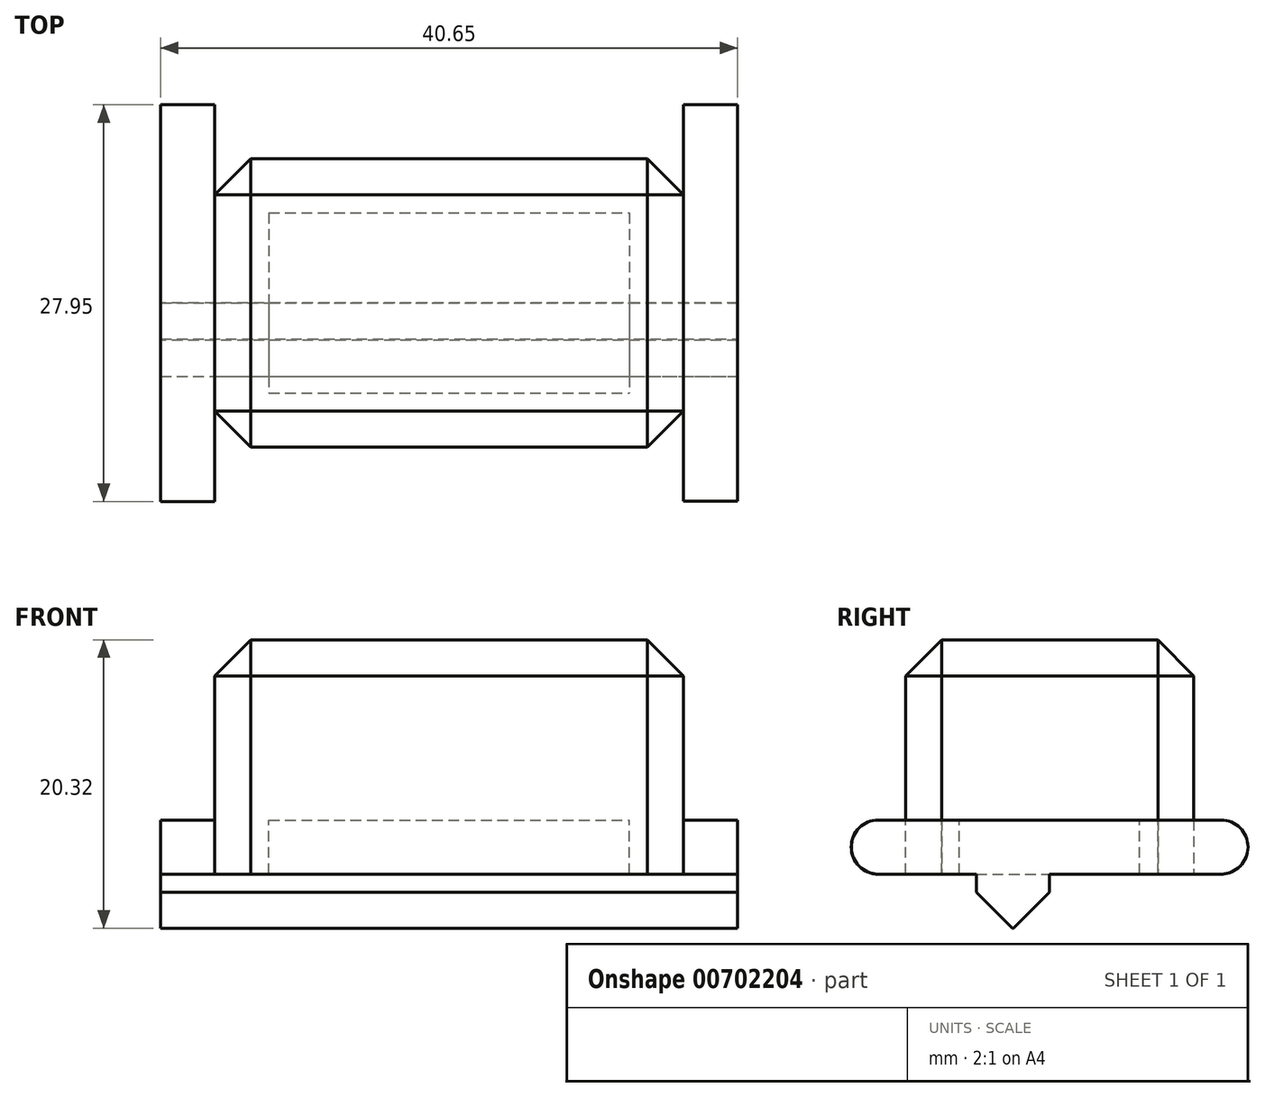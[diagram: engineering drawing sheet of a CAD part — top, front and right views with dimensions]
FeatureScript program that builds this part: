
annotation { "Feature Type Name" : "Feature", "Feature Type Description" : "" }
export const myFeature = defineFeature(function(context is Context, id is Id, definition is map)
    precondition{}
    {
        {
            var Q0;
            Q0=qCreatedBy(makeId("Top.planeOp"),FACE);
            var sketch = newSketch(context, id + "F0", { "sketchPlane" : qUnion([Q0])});
            skLineSegment(sketch, "E0.bottom", {"start": v(0, 0) * mm, "end": v(33.02, 0) * mm});
            skLineSegment(sketch, "E0.top", {"start": v(0, -20.32) * mm, "end": v(33.02, -20.32) * mm});
            skLineSegment(sketch, "E0.left", {"start": v(0, 0) * mm, "end": v(0, -20.32) * mm});
            skLineSegment(sketch, "E0.right", {"start": v(33.02, 0) * mm, "end": v(33.02, -20.32) * mm});
            skLineSegment(sketch, "E1", {"start": v(0, 0) * mm, "end": v(3.81, 0) * mm});
            skLineSegment(sketch, "E2.bottom", {"start": v(3.81, -3.81) * mm, "end": v(29.21, -3.81) * mm});
            skLineSegment(sketch, "E2.top", {"start": v(3.81, -16.51) * mm, "end": v(29.21, -16.51) * mm});
            skLineSegment(sketch, "E2.left", {"start": v(3.81, -3.81) * mm, "end": v(3.81, -16.51) * mm});
            skLineSegment(sketch, "E2.right", {"start": v(29.21, -3.8) * mm, "end": v(29.21, -16.51) * mm});
            skSolve(sketch);
        }
        {
            var Q0;
            Q0 = qSketchRegion(id + "F0", true);
            extrude(context, id + "F1", {"entities" : qUnion([Q0]), "oppositeDirection" : true, "depth" : 3.8 * mm, "offsetDistance" : 25.4 * mm});
        }
        {
            var Q0;
            Q0=qCreatedBy(makeId("Top.planeOp"),FACE);
            var sketch = newSketch(context, id + "F2", { "sketchPlane" : qUnion([Q0])});
            skLineSegment(sketch, "E3.bottom", {"start": v(0, 0) * mm, "end": v(33.02, 0) * mm});
            skLineSegment(sketch, "E3.top", {"start": v(0, -20.32) * mm, "end": v(33.02, -20.32) * mm});
            skLineSegment(sketch, "E3.left", {"start": v(0, 0) * mm, "end": v(0, -20.32) * mm});
            skLineSegment(sketch, "E3.right", {"start": v(33.02, 0) * mm, "end": v(33.02, -20.32) * mm});
            skSolve(sketch);
        }
        {
            var Q0;
            Q0 = qSketchRegion(id + "F2", true);
            extrude(context, id + "F3", {"entities" : qUnion([Q0]), "operationType" : NewBodyOperationType.ADD, "depth" : 12.7 * mm, "offsetDistance" : 25.4 * mm});
        }
        {
            var Q0;
            Q0=makeQuery(id+"F3.opExtrude","CAP_EDGE",EDGE,{"disambiguationData":[OSD([sQuery(id+"F2.wireOp",EDGE,"E3.bottom")])],"isStart":false});
            var Q1;
            Q1=makeQuery(id+"F3.opExtrude","CAP_EDGE",EDGE,{"disambiguationData":[OSD([sQuery(id+"F2.wireOp",EDGE,"E3.right")])],"isStart":false});
            var Q2;
            Q2=makeQuery(id+"F3.opExtrude","CAP_EDGE",EDGE,{"disambiguationData":[OSD([sQuery(id+"F2.wireOp",EDGE,"E3.top")])],"isStart":false});
            var Q3;
            Q3=makeQuery(id+"F3.opExtrude","CAP_EDGE",EDGE,{"disambiguationData":[OSD([sQuery(id+"F2.wireOp",EDGE,"E3.left")])],"isStart":false});
            var Q4;
            Q4=makeQuery(id+"F3.boolean.opBoolean","MERGE",EDGE,{"derivedFrom":[makeQuery(id+"F1.opExtrude","SWEPT_EDGE",EDGE,{"disambiguationData":[OSD([sQuery(id+"F0.wireOp",EDGE,"E0.bottom"),sQuery(id+"F0.wireOp",EDGE,"E0.right")])]}),makeQuery(id+"F3.opExtrude","SWEPT_EDGE",EDGE,{"disambiguationData":[OSD([sQuery(id+"F2.wireOp",EDGE,"E3.bottom"),sQuery(id+"F2.wireOp",EDGE,"E3.right")])]})]});
            var Q5;
            Q5=makeQuery(id+"F3.boolean.opBoolean","MERGE",EDGE,{"derivedFrom":[makeQuery(id+"F1.opExtrude","SWEPT_EDGE",EDGE,{"disambiguationData":[OSD([sQuery(id+"F0.wireOp",EDGE,"E0.left"),sQuery(id+"F0.wireOp",EDGE,"E1")])]}),makeQuery(id+"F3.opExtrude","SWEPT_EDGE",EDGE,{"disambiguationData":[OSD([sQuery(id+"F2.wireOp",EDGE,"E3.bottom"),sQuery(id+"F2.wireOp",EDGE,"E3.left")])]})]});
            var Q6;
            Q6=makeQuery(id+"F3.boolean.opBoolean","MERGE",EDGE,{"derivedFrom":[makeQuery(id+"F1.opExtrude","SWEPT_EDGE",EDGE,{"disambiguationData":[OSD([sQuery(id+"F0.wireOp",EDGE,"E0.top"),sQuery(id+"F0.wireOp",EDGE,"E0.right")])]}),makeQuery(id+"F3.opExtrude","SWEPT_EDGE",EDGE,{"disambiguationData":[OSD([sQuery(id+"F2.wireOp",EDGE,"E3.top"),sQuery(id+"F2.wireOp",EDGE,"E3.right")])]})]});
            var Q7;
            Q7=makeQuery(id+"F3.boolean.opBoolean","MERGE",EDGE,{"derivedFrom":[makeQuery(id+"F1.opExtrude","SWEPT_EDGE",EDGE,{"disambiguationData":[OSD([sQuery(id+"F0.wireOp",EDGE,"E0.top"),sQuery(id+"F0.wireOp",EDGE,"E0.left")])]}),makeQuery(id+"F3.opExtrude","SWEPT_EDGE",EDGE,{"disambiguationData":[OSD([sQuery(id+"F2.wireOp",EDGE,"E3.top"),sQuery(id+"F2.wireOp",EDGE,"E3.left")])]})]});
            chamfer(context, id + "F4", {"entities" : qUnion([Q0, Q1, Q2, Q3, Q4, Q5, Q6, Q7]), "width" : 2.54 * mm, "tangentPropagation" : true});
        }
        {
            var Q0;
            Q0=makeQuery(id+"F3.boolean.opBoolean","MERGE",FACE,{"derivedFrom":[makeQuery(id+"F1.opExtrude","SWEPT_FACE",FACE,{"disambiguationData":[OSD([sQuery(id+"F0.wireOp",EDGE,"E0.left")])]}),makeQuery(id+"F3.opExtrude","SWEPT_FACE",FACE,{"disambiguationData":[OSD([sQuery(id+"F2.wireOp",EDGE,"E3.left")])]})]});
            var sketch = newSketch(context, id + "F5", { "sketchPlane" : qUnion([Q0])});
            skLineSegment(sketch, "E4", {"start": v(0, 0) * mm, "end": v(-3.8, 0) * mm});
            skLineSegment(sketch, "E5", {"start": v(-3.8, 0) * mm, "end": v(-3.8, -3.82) * mm});
            skLineSegment(sketch, "E6", {"start": v(-3.8, -3.82) * mm, "end": v(24.14, -3.82) * mm});
            skLineSegment(sketch, "E7", {"start": v(24.14, -3.82) * mm, "end": v(24.14, 0) * mm});
            skLineSegment(sketch, "E8", {"start": v(24.14, 0) * mm, "end": v(0, 0) * mm});
            skSolve(sketch);
        }
        {
            var Q0;
            Q0 = qSketchRegion(id + "F5", true);
            extrude(context, id + "F6", {"entities" : qUnion([Q0]), "operationType" : NewBodyOperationType.ADD, "depth" : 3.8 * mm, "offsetDistance" : 25.4 * mm});
        }
        {
            var Q0;
            Q0=makeQuery(id+"F3.boolean.opBoolean","MERGE",FACE,{"derivedFrom":[makeQuery(id+"F1.opExtrude","SWEPT_FACE",FACE,{"disambiguationData":[OSD([sQuery(id+"F0.wireOp",EDGE,"E0.right")])]}),makeQuery(id+"F3.opExtrude","SWEPT_FACE",FACE,{"disambiguationData":[OSD([sQuery(id+"F2.wireOp",EDGE,"E3.right")])]})]});
            var sketch = newSketch(context, id + "F7", { "sketchPlane" : qUnion([Q0])});
            skLineSegment(sketch, "E9", {"start": v(0, 0) * mm, "end": v(3.81, 0) * mm});
            skLineSegment(sketch, "E10.bottom", {"start": v(3.81, 0) * mm, "end": v(-24.13, 0) * mm});
            skLineSegment(sketch, "E10.top", {"start": v(3.81, -3.8) * mm, "end": v(-24.13, -3.81) * mm});
            skLineSegment(sketch, "E10.left", {"start": v(3.81, 0) * mm, "end": v(3.81, -3.8) * mm});
            skLineSegment(sketch, "E10.right", {"start": v(-24.13, 0) * mm, "end": v(-24.13, -3.81) * mm});
            skSolve(sketch);
        }
        {
            var Q0;
            Q0 = qSketchRegion(id + "F7", true);
            extrude(context, id + "F8", {"entities" : qUnion([Q0]), "operationType" : NewBodyOperationType.ADD, "depth" : 3.8 * mm, "offsetDistance" : 25.4 * mm});
        }
        {
            var Q0;
            Q0=makeQuery(id+"F8.opExtrude","SWEPT_EDGE",EDGE,{"disambiguationData":[OSD([sQuery(id+"F7.wireOp",EDGE,"E10.bottom"),sQuery(id+"F7.wireOp",EDGE,"E10.left")])]});
            var Q1;
            Q1=makeQuery(id+"F8.opExtrude","SWEPT_EDGE",EDGE,{"disambiguationData":[OSD([sQuery(id+"F7.wireOp",EDGE,"E10.top"),sQuery(id+"F7.wireOp",EDGE,"E10.left")])]});
            var Q2;
            Q2=makeQuery(id+"F8.opExtrude","SWEPT_EDGE",EDGE,{"disambiguationData":[OSD([sQuery(id+"F7.wireOp",EDGE,"E10.bottom"),sQuery(id+"F7.wireOp",EDGE,"E10.right")])]});
            var Q3;
            Q3=makeQuery(id+"F6.opExtrude","SWEPT_EDGE",EDGE,{"disambiguationData":[OSD([sQuery(id+"F5.wireOp",EDGE,"E4"),sQuery(id+"F5.wireOp",EDGE,"E5")])]});
            var Q4;
            Q4=makeQuery(id+"F6.opExtrude","SWEPT_EDGE",EDGE,{"disambiguationData":[OSD([sQuery(id+"F5.wireOp",EDGE,"E5"),sQuery(id+"F5.wireOp",EDGE,"E6")])]});
            var Q5;
            Q5=makeQuery(id+"F6.opExtrude","SWEPT_EDGE",EDGE,{"disambiguationData":[OSD([sQuery(id+"F5.wireOp",EDGE,"E7"),sQuery(id+"F5.wireOp",EDGE,"E8")])]});
            var Q6;
            Q6=makeQuery(id+"F6.opExtrude","SWEPT_EDGE",EDGE,{"disambiguationData":[OSD([sQuery(id+"F5.wireOp",EDGE,"E6"),sQuery(id+"F5.wireOp",EDGE,"E7")])]});
            var Q7;
            Q7=makeQuery(id+"F8.opExtrude","SWEPT_EDGE",EDGE,{"disambiguationData":[OSD([sQuery(id+"F7.wireOp",EDGE,"E10.top"),sQuery(id+"F7.wireOp",EDGE,"E10.right")])]});
            fillet(context, id + "F9", {"entities" : qUnion([Q0, Q1, Q2, Q3, Q4, Q5, Q6, Q7]), "radius" : 1.9 * mm, "tangentPropagation" : true, "allowEdgeOverflow" : false});
        }
        {
            var Q0;
            Q0=makeQuery(id+"F8.boolean.opBoolean","MERGE",FACE,{"derivedFrom":[makeQuery(id+"F1.opExtrude","CAP_FACE",FACE,{"disambiguationData":[OSD([sQuery(id+"F0.wireOp",EDGE,"E0.bottom"),sQuery(id+"F0.wireOp",EDGE,"E0.top"),sQuery(id+"F0.wireOp",EDGE,"E0.left"),sQuery(id+"F0.wireOp",EDGE,"E0.right"),sQuery(id+"F0.wireOp",EDGE,"E1"),sQuery(id+"F0.wireOp",EDGE,"E2.bottom"),sQuery(id+"F0.wireOp",EDGE,"E2.top"),sQuery(id+"F0.wireOp",EDGE,"E2.left"),sQuery(id+"F0.wireOp",EDGE,"E2.right")])],"isStart":false}),makeQuery(id+"F8.opExtrude","SWEPT_FACE",FACE,{"disambiguationData":[OSD([sQuery(id+"F7.wireOp",EDGE,"E10.top")])]})]});
            var sketch = newSketch(context, id + "F10", { "sketchPlane" : qUnion([Q0])});
            skLineSegment(sketch, "E11.bottom", {"start": v(-3.96, 15.33) * mm, "end": v(36.83, 15.33) * mm});
            skLineSegment(sketch, "E11.top", {"start": v(-3.96, 10.16) * mm, "end": v(36.83, 10.16) * mm});
            skLineSegment(sketch, "E11.left", {"start": v(-3.96, 15.33) * mm, "end": v(-3.96, 10.16) * mm});
            skLineSegment(sketch, "E11.right", {"start": v(36.83, 15.33) * mm, "end": v(36.83, 10.16) * mm});
            skSolve(sketch);
        }
        {
            var Q0;
            Q0 = qSketchRegion(id + "F10", true);
            extrude(context, id + "F11", {"entities" : qUnion([Q0]), "operationType" : NewBodyOperationType.ADD, "depth" : 3.8 * mm, "offsetDistance" : 25.4 * mm});
        }
        {
            var Q0;
            Q0=makeQuery(id+"F11.opExtrude","CAP_EDGE",EDGE,{"disambiguationData":[OSD([sQuery(id+"F10.wireOp",EDGE,"E11.bottom")])],"isStart":false});
            var Q1;
            Q1=makeQuery(id+"F11.opExtrude","CAP_EDGE",EDGE,{"disambiguationData":[OSD([sQuery(id+"F10.wireOp",EDGE,"E11.top")])],"isStart":false});
            chamfer(context, id + "F12", {"entities" : qUnion([Q0, Q1]), "width" : 2.54 * mm, "tangentPropagation" : true});
        }
        {
            var Q0;
            Q0=makeQuery(id+"F3.opExtrude","CAP_FACE",FACE,{"disambiguationData":[OSD([sQuery(id+"F2.wireOp",EDGE,"E3.bottom"),sQuery(id+"F2.wireOp",EDGE,"E3.top"),sQuery(id+"F2.wireOp",EDGE,"E3.left"),sQuery(id+"F2.wireOp",EDGE,"E3.right")])],"isStart":false});
            var sketch = newSketch(context, id + "F13", { "sketchPlane" : qUnion([Q0])});
            skLineSegment(sketch, "E12.bottom", {"start": v(-4, -10.1) * mm, "end": v(-3.82, -10.1) * mm});
            skLineSegment(sketch, "E12.top", {"start": v(-4, -15.55) * mm, "end": v(-3.82, -15.55) * mm});
            skLineSegment(sketch, "E12.left", {"start": v(-4, -10.1) * mm, "end": v(-4, -15.55) * mm});
            skLineSegment(sketch, "E12.right", {"start": v(-3.82, -10.1) * mm, "end": v(-3.82, -15.55) * mm});
            skSolve(sketch);
        }
        {
            var Q0;
            Q0 = qSketchRegion(id + "F13", true);
            extrude(context, id + "F14", {"entities" : qUnion([Q0]), "operationType" : NewBodyOperationType.REMOVE, "oppositeDirection" : true, "depth" : 101.6 * mm, "offsetDistance" : 25.4 * mm});
        }
    });
